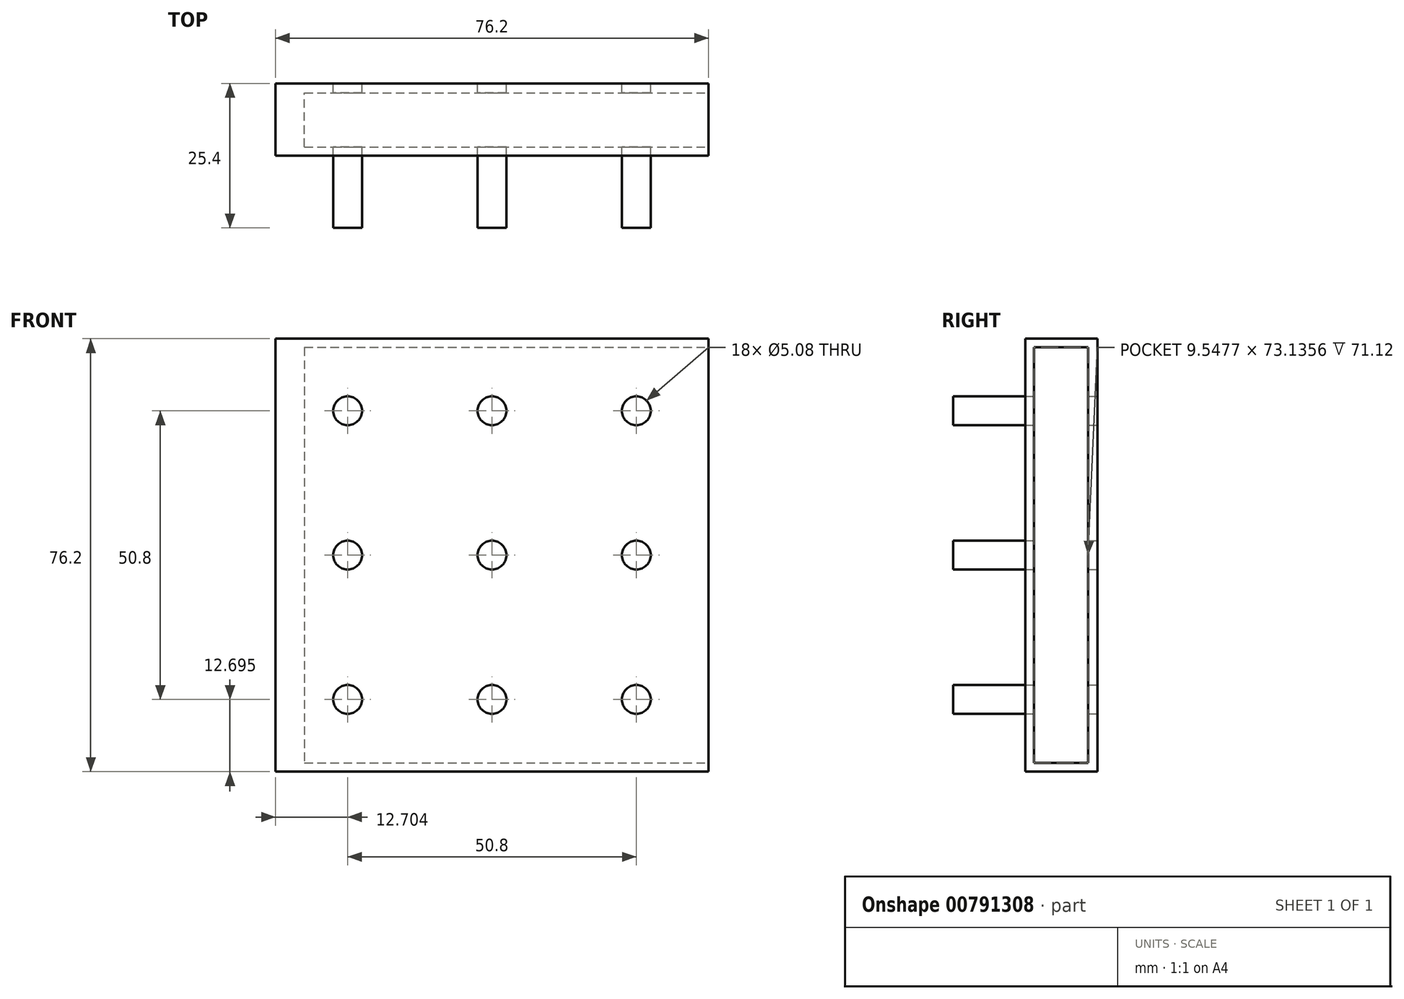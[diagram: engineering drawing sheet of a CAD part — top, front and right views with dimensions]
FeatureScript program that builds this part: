
annotation { "Feature Type Name" : "Feature", "Feature Type Description" : "" }
export const myFeature = defineFeature(function(context is Context, id is Id, definition is map)
    precondition{}
    {
        {
            var Q0;
            Q0=qCreatedBy(makeId("Front.planeOp"),FACE);
            var sketch = newSketch(context, id + "F0", { "sketchPlane" : qUnion([Q0])});
            skLineSegment(sketch, "E0", {"start": v(-44.2, 40.2) * mm, "end": v(-44.2, 14.8) * mm});
            skLineSegment(sketch, "E1", {"start": v(-44.2, 14.8) * mm, "end": v(-40.77, 14.8) * mm});
            skLineSegment(sketch, "E2", {"start": v(-40.77, 14.8) * mm, "end": v(-44.2, 14.8) * mm});
            skLineSegment(sketch, "E3", {"start": v(-44.2, 14.8) * mm, "end": v(-44.2, -10.6) * mm});
            skLineSegment(sketch, "E4", {"start": v(-44.2, -10.6) * mm, "end": v(-44.2, -36) * mm});
            skLineSegment(sketch, "E5", {"start": v(-44.2, -36) * mm, "end": v(-18.8, -36) * mm});
            skLineSegment(sketch, "E6", {"start": v(-18.8, -36) * mm, "end": v(6.6, -36) * mm});
            skLineSegment(sketch, "E7", {"start": v(6.6, -36) * mm, "end": v(32, -36) * mm});
            skLineSegment(sketch, "E8", {"start": v(32, -36) * mm, "end": v(32, 40.2) * mm});
            skLineSegment(sketch, "E9", {"start": v(32, 40.2) * mm, "end": v(-44.2, 40.2) * mm});
            skLineSegment(sketch, "E10", {"start": v(-40.77, 14.8) * mm, "end": v(32, 14.8) * mm});
            skLineSegment(sketch, "E11", {"start": v(-44.2, -10.6) * mm, "end": v(32, -10.6) * mm});
            skLineSegment(sketch, "E12", {"start": v(-18.8, -36) * mm, "end": v(-18.8, 40.2) * mm});
            skLineSegment(sketch, "E13", {"start": v(6.6, -36) * mm, "end": v(6.6, 40.2) * mm});
            skPoint(sketch, "E14.startSnap0", {"position": v(-6.1, 40.2) * mm});
            skCircle(sketch, "E15", {"center": v(-6.1, 27.5) * mm, "radius": 2.54 * mm});
            skCircle(sketch, "E16", {"center": v(19.3, 27.5) * mm, "radius": 2.54 * mm});
            skCircle(sketch, "E17", {"center": v(-31.5, 27.5) * mm, "radius": 2.54 * mm});
            skCircle(sketch, "E18", {"center": v(-31.5, 2.1) * mm, "radius": 2.54 * mm});
            skCircle(sketch, "E19", {"center": v(-6.1, 2.1) * mm, "radius": 2.54 * mm});
            skCircle(sketch, "E20", {"center": v(19.3, 2.1) * mm, "radius": 2.54 * mm});
            skCircle(sketch, "E21", {"center": v(19.3, -23.3) * mm, "radius": 2.54 * mm});
            skCircle(sketch, "E22", {"center": v(-6.1, -23.3) * mm, "radius": 2.54 * mm});
            skCircle(sketch, "E23", {"center": v(-31.5, -23.3) * mm, "radius": 2.54 * mm});
            skSolve(sketch);
        }
        {
            var Q0;
            Q0=makeQuery(id+"F0.imprint","IMPRINT",FACE,{"disambiguationData":[TD([[makeQuery(id+"F0.imprint","IMPRINT",EDGE,{"derivedFrom":sQuery(id+"F0.wireOp",EDGE,"E17")}),1.0]])]});
            var Q1;
            Q1=makeQuery(id+"F0.imprint","IMPRINT",FACE,{"disambiguationData":[TD([[makeQuery(id+"F0.imprint","IMPRINT",EDGE,{"derivedFrom":sQuery(id+"F0.wireOp",EDGE,"E15")}),1.0]])]});
            var Q2;
            Q2=makeQuery(id+"F0.imprint","IMPRINT",FACE,{"disambiguationData":[TD([[makeQuery(id+"F0.imprint","IMPRINT",EDGE,{"derivedFrom":sQuery(id+"F0.wireOp",EDGE,"E16")}),1.0]])]});
            var Q3;
            Q3=makeQuery(id+"F0.imprint","IMPRINT",FACE,{"disambiguationData":[TD([[makeQuery(id+"F0.imprint","IMPRINT",EDGE,{"derivedFrom":sQuery(id+"F0.wireOp",EDGE,"E18")}),1.0]])]});
            var Q4;
            Q4=makeQuery(id+"F0.imprint","IMPRINT",FACE,{"disambiguationData":[TD([[makeQuery(id+"F0.imprint","IMPRINT",EDGE,{"derivedFrom":sQuery(id+"F0.wireOp",EDGE,"E19")}),1.0]])]});
            var Q5;
            Q5=makeQuery(id+"F0.imprint","IMPRINT",FACE,{"disambiguationData":[TD([[makeQuery(id+"F0.imprint","IMPRINT",EDGE,{"derivedFrom":sQuery(id+"F0.wireOp",EDGE,"E20")}),1.0]])]});
            var Q6;
            Q6=makeQuery(id+"F0.imprint","IMPRINT",FACE,{"disambiguationData":[TD([[makeQuery(id+"F0.imprint","IMPRINT",EDGE,{"derivedFrom":sQuery(id+"F0.wireOp",EDGE,"E23")}),1.0]])]});
            var Q7;
            Q7=makeQuery(id+"F0.imprint","IMPRINT",FACE,{"disambiguationData":[TD([[makeQuery(id+"F0.imprint","IMPRINT",EDGE,{"derivedFrom":sQuery(id+"F0.wireOp",EDGE,"E22")}),1.0]])]});
            var Q8;
            Q8=makeQuery(id+"F0.imprint","IMPRINT",FACE,{"disambiguationData":[TD([[makeQuery(id+"F0.imprint","IMPRINT",EDGE,{"derivedFrom":sQuery(id+"F0.wireOp",EDGE,"E21")}),1.0]])]});
            extrude(context, id + "F1", {"entities" : qUnion([Q0, Q1, Q2, Q3, Q4, Q5, Q6, Q7, Q8]), "depth" : 25.4 * mm, "offsetDistance" : 25.4 * mm});
        }
        {
            var Q0;
            Q0 = qSketchRegion(id + "F0", true);
            var Q1;
            Q1=makeQuery(id+"F0.imprint","IMPRINT",FACE,{"disambiguationData":[TD([[makeQuery(id+"F0.imprint","IMPRINT",EDGE,{"derivedFrom":sQuery(id+"F0.wireOp",EDGE,"E19")}),-1.0]])]});
            extrude(context, id + "F2", {"entities" : qUnion([Q0, Q1]), "depth" : 12.7 * mm, "offsetDistance" : 25.4 * mm});
        }
        {
            var Q0;
            Q0=makeQuery(id+"F2.opExtrude","SWEPT_FACE",FACE,{"disambiguationData":[OSD([sQuery(id+"F0.wireOp",EDGE,"E8")])]});
            var sketch = newSketch(context, id + "F3", { "sketchPlane" : qUnion([Q0])});
            skLineSegment(sketch, "E24.bottom", {"start": v(-11.17, 38.67) * mm, "end": v(-1.62, 38.67) * mm});
            skLineSegment(sketch, "E24.top", {"start": v(-11.17, -34.47) * mm, "end": v(-1.62, -34.47) * mm});
            skLineSegment(sketch, "E24.left", {"start": v(-11.17, 38.67) * mm, "end": v(-11.17, -34.47) * mm});
            skLineSegment(sketch, "E24.right", {"start": v(-1.62, 38.67) * mm, "end": v(-1.62, -34.47) * mm});
            skSolve(sketch);
        }
        {
            var Q0;
            Q0 = qSketchRegion(id + "F3", true);
            extrude(context, id + "F4", {"entities" : qUnion([Q0]), "operationType" : NewBodyOperationType.REMOVE, "oppositeDirection" : true, "depth" : 71.12 * mm, "offsetDistance" : 25.4 * mm});
        }
    });
